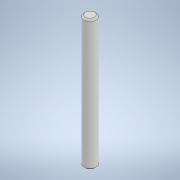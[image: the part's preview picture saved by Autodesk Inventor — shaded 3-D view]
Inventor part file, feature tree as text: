
AUTODESK INVENTOR PART (.ipt)
format: ipt  version: 2020 (Build 240168000, 168)  size: 96,768 bytes
history: native  units: in
note: dims shown in document units (in); Inventor stores cm internally (conversion verified against a paired STEP export)
features: chamfer x2, extrude x1, sketch x1
ambient origin geometry x8: Origin, YZ Plane, XZ Plane, XY Plane, X Axis, Y Axis, Z Axis, Center Point
bodies: Solid1 (feature_tree)
feature tree (4):
  extrude  "Extrusion1"  Depth=4.0in TaperAngle=0.0deg
  chamfer  "Chamfer1"  Distance=0.05in Angle=45.0deg
  chamfer  "Chamfer2"  Distance=0.05in Angle=45.0deg
  sketch  "Sketch1"  dims[d0=0.375in d1=4.0in d2=0.0in d3=0.05in d4=0.125in d5=45.0deg d6=0.05in d7=0.125in d8=45.0deg]
